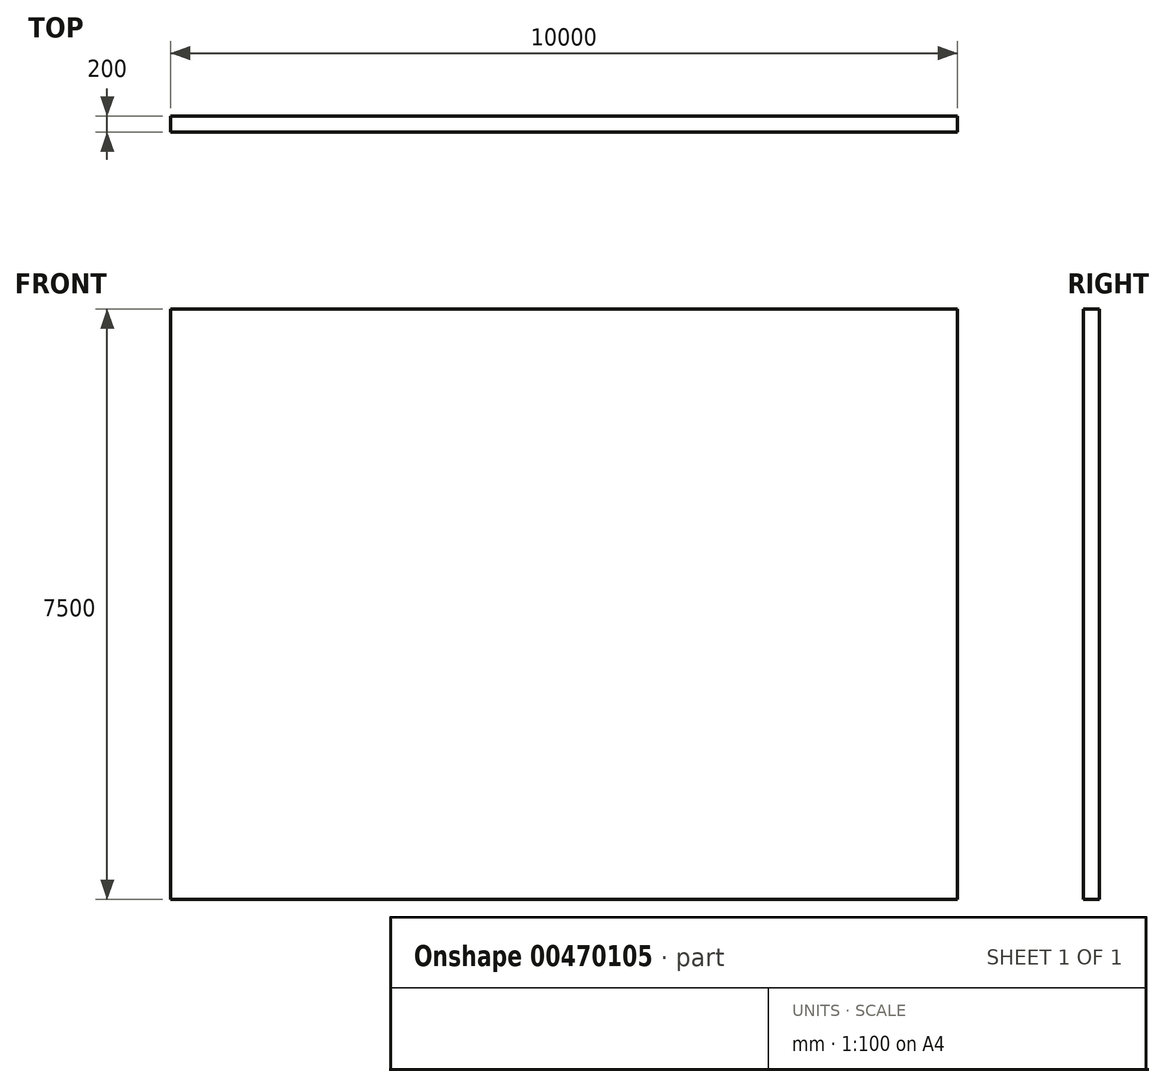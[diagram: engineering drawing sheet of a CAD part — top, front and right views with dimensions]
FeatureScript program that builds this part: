
annotation { "Feature Type Name" : "Feature", "Feature Type Description" : "" }
export const myFeature = defineFeature(function(context is Context, id is Id, definition is map)
    precondition{}
    {
        {
            var Q0;
            Q0=qCreatedBy(makeId("Front.planeOp"),FACE);
            var sketch = newSketch(context, id + "F0", { "sketchPlane" : qUnion([Q0])});
            skLineSegment(sketch, "E0.bottom", {"start": v(0, 7500) * mm, "end": v(10000, 7500) * mm});
            skLineSegment(sketch, "E0.top", {"start": v(0, 0) * mm, "end": v(10000, 0) * mm});
            skLineSegment(sketch, "E0.left", {"start": v(0, 7500) * mm, "end": v(0, 0) * mm});
            skLineSegment(sketch, "E0.right", {"start": v(10000, 7500) * mm, "end": v(10000, 0) * mm});
            skSolve(sketch);
        }
        {
            var Q0;
            Q0=makeQuery(id+"F0.imprint","IMPRINT",FACE,{"disambiguationData":[TD([[makeQuery(id+"F0.imprint","IMPRINT",EDGE,{"derivedFrom":sQuery(id+"F0.wireOp",EDGE,"E0.bottom")}),-1.0]])]});
            var Q1;
            Q1=sQuery(id+"F0.wireOp",EDGE,"E0.bottom");
            var Q2;
            Q2=sQuery(id+"F0.wireOp",EDGE,"E0.right");
            var Q3;
            Q3=sQuery(id+"F0.wireOp",EDGE,"E0.top");
            var Q4;
            Q4=sQuery(id+"F0.wireOp",EDGE,"E0.left");
            extrude(context, id + "F1", {"entities" : qUnion([Q0]), "bodyType" : ToolBodyType.SURFACE, "surfaceEntities" : qUnion([Q1, Q2, Q3, Q4]), "oppositeDirection" : true, "depth" : 200 * mm, "offsetDistance" : 25 * mm});
        }
    });
